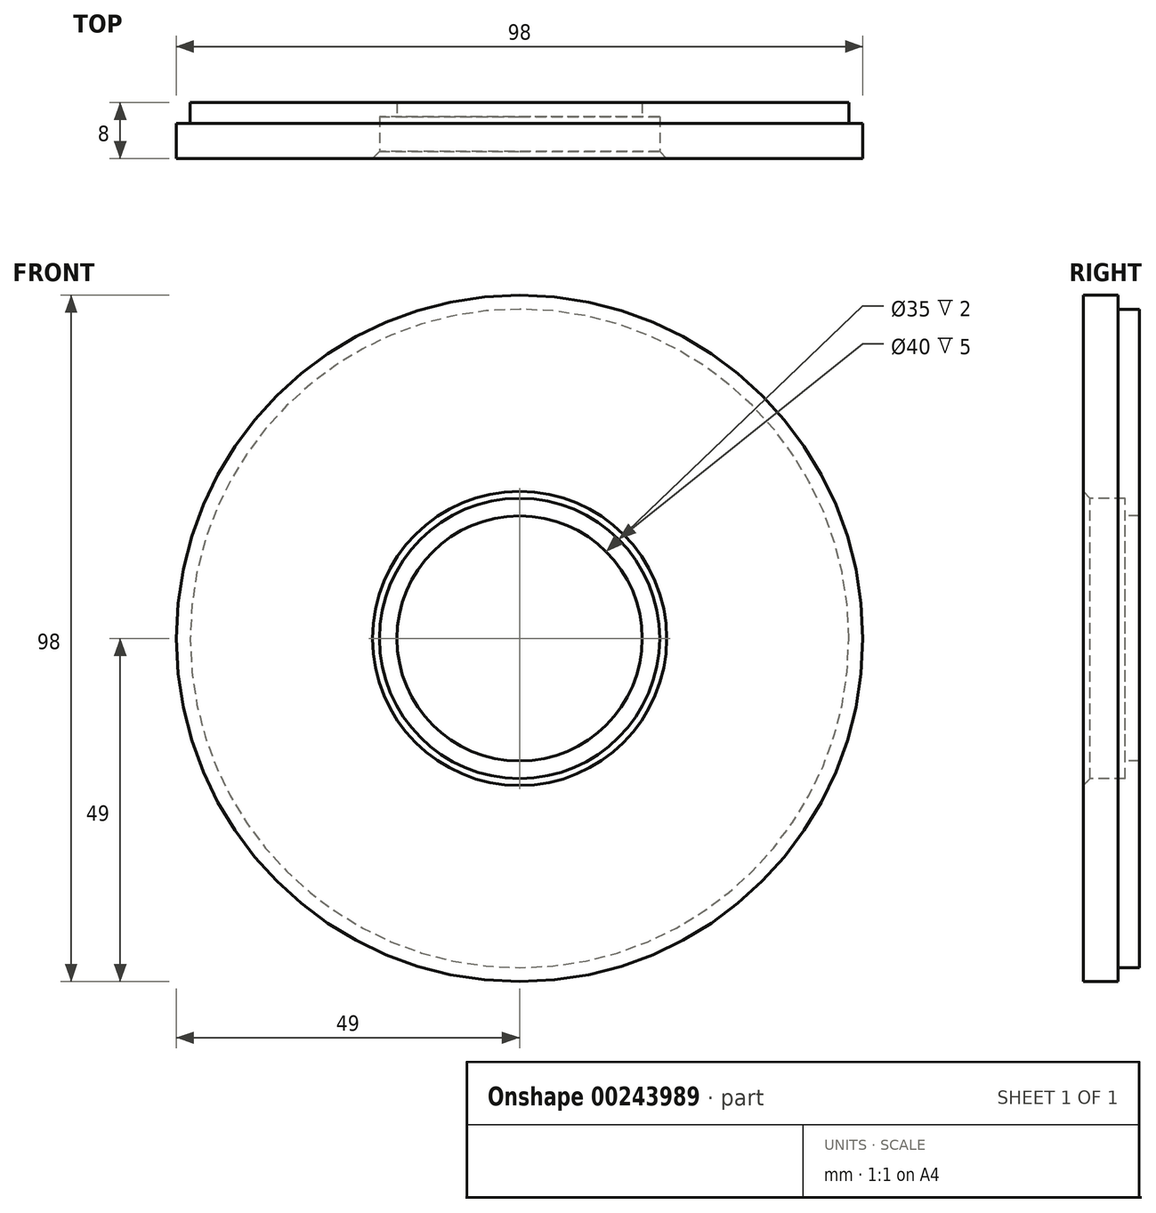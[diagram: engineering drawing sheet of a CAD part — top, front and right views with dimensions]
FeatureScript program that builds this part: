
annotation { "Feature Type Name" : "Feature", "Feature Type Description" : "" }
export const myFeature = defineFeature(function(context is Context, id is Id, definition is map)
    precondition{}
    {
        {
            var Q0;
            Q0=qCreatedBy(makeId("Top.planeOp"),FACE);
            var sketch = newSketch(context, id + "F0", { "sketchPlane" : qUnion([Q0])});
            skLineSegment(sketch, "E0", {"start": v(49, 0) * mm, "end": v(49, 5) * mm});
            skLineSegment(sketch, "E1", {"start": v(49, 5) * mm, "end": v(47, 5) * mm});
            skLineSegment(sketch, "E2", {"start": v(47, 5) * mm, "end": v(47, 8) * mm});
            skLineSegment(sketch, "E3", {"start": v(47, 8) * mm, "end": v(17.5, 8) * mm});
            skLineSegment(sketch, "E4", {"start": v(17.5, 8) * mm, "end": v(17.5, 6) * mm});
            skLineSegment(sketch, "E5", {"start": v(17.5, 6) * mm, "end": v(20, 6) * mm});
            skLineSegment(sketch, "E6", {"start": v(20, 6) * mm, "end": v(20, 0) * mm});
            skLineSegment(sketch, "E7", {"start": v(20, 0) * mm, "end": v(49, 0) * mm});
            skLineSegment(sketch, "E8", {"start": v(0, 0) * mm, "end": v(0, 340.23) * mm, "construction": true});
            skSolve(sketch);
        }
        {
            var Q0;
            Q0=makeQuery(id+"F0.imprint","IMPRINT",FACE,{"disambiguationData":[TD([[makeQuery(id+"F0.imprint","IMPRINT",EDGE,{"derivedFrom":sQuery(id+"F0.wireOp",EDGE,"E0")}),1.0]])]});
            var Q1;
            Q1=sQuery(id+"F0.wireOp",EDGE,"E8");
            revolve(context, id + "F1", {"entities" : qUnion([Q0]), "axis" : qUnion([Q1]), "revolveType" : RevolveType.FULL});
        }
        {
            var Q0;
            Q0=makeQuery(id+"F1.opRevolve","SWEPT_EDGE",EDGE,{"disambiguationData":[OSD([sQuery(id+"F0.wireOp",EDGE,"E6"),sQuery(id+"F0.wireOp",EDGE,"E7")])]});
            chamfer(context, id + "F2", {"entities" : qUnion([Q0]), "width" : 1 * mm, "tangentPropagation" : true});
        }
    });
